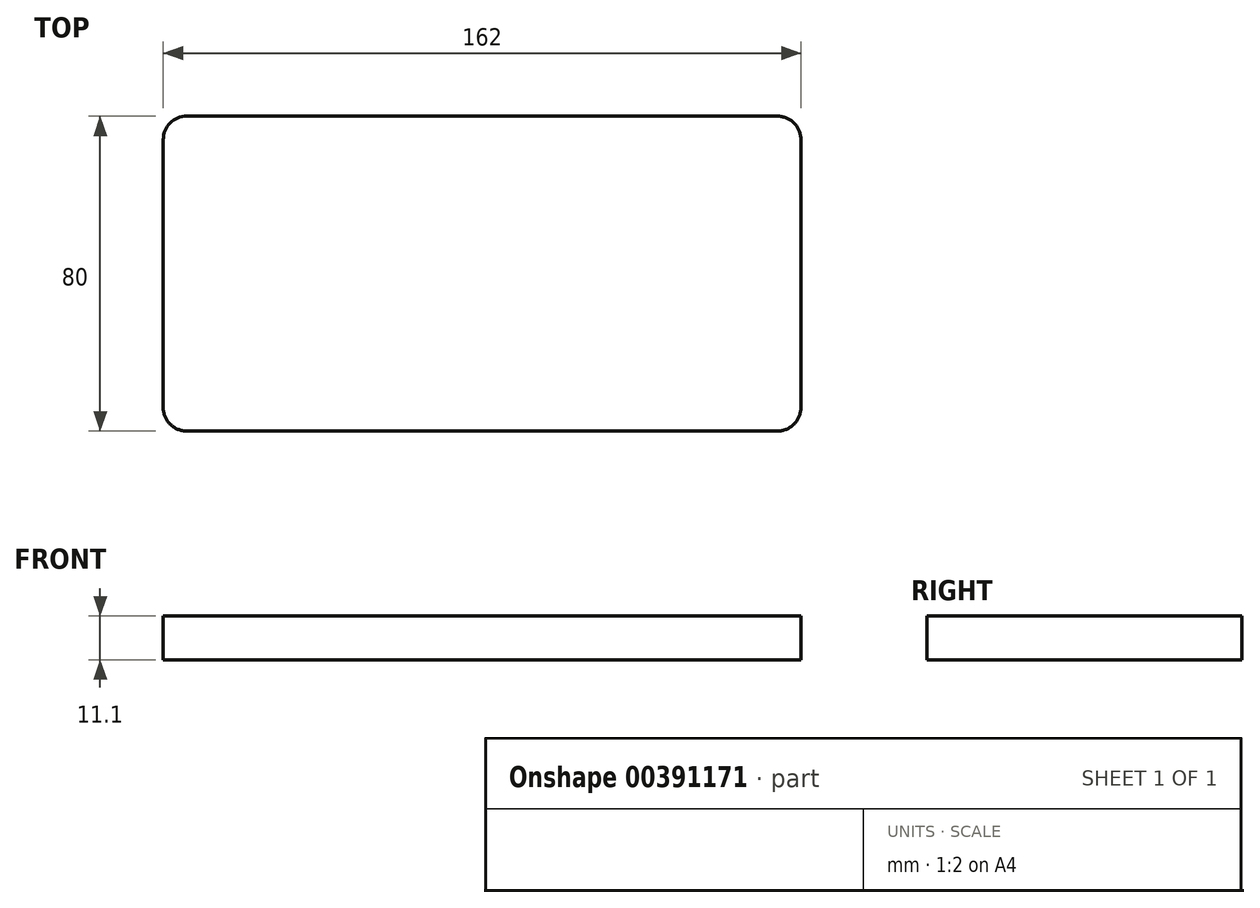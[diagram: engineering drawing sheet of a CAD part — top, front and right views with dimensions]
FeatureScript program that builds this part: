
annotation { "Feature Type Name" : "Feature", "Feature Type Description" : "" }
export const myFeature = defineFeature(function(context is Context, id is Id, definition is map)
    precondition{}
    {
        {
            var Q0;
            Q0=qCreatedBy(makeId("Top.planeOp"),FACE);
            var sketch = newSketch(context, id + "F0", { "sketchPlane" : qUnion([Q0])});
            skPoint(sketch, "E0.middle", {"position": v(0, 0) * mm});
            skLineSegment(sketch, "E1", {"start": v(-75, 40) * mm, "end": v(75, 40) * mm});
            skLineSegment(sketch, "E2", {"start": v(81, 34) * mm, "end": v(81, -34) * mm});
            skLineSegment(sketch, "E3", {"start": v(75, -40) * mm, "end": v(-75, -40) * mm});
            skLineSegment(sketch, "E4", {"start": v(-81, -34) * mm, "end": v(-81, 34) * mm});
            skArc(sketch, "E5", {"start": v(-81, 34) * mm, "mid": v(-79.24, 38.24) * mm, "end": v(-75, 40) * mm});
            skArc(sketch, "E6", {"start": v(-75, -40) * mm, "mid": v(-79.25, -38.24) * mm, "end": v(-81, -34) * mm});
            skArc(sketch, "E7", {"start": v(75, -40) * mm, "mid": v(79.24, -38.24) * mm, "end": v(81, -34) * mm});
            skArc(sketch, "E8", {"start": v(81, 34) * mm, "mid": v(79.24, 38.24) * mm, "end": v(75, 40) * mm});
            skSolve(sketch);
        }
        {
            var Q0;
            Q0=makeQuery(id+"F0.imprint","IMPRINT",FACE,{"disambiguationData":[TD([[makeQuery(id+"F0.imprint","IMPRINT",EDGE,{"derivedFrom":sQuery(id+"F0.wireOp",EDGE,"E1")}),-1.0]])]});
            extrude(context, id + "F1", {"entities" : qUnion([Q0]), "depth" : 11.1 * mm});
        }
    });
